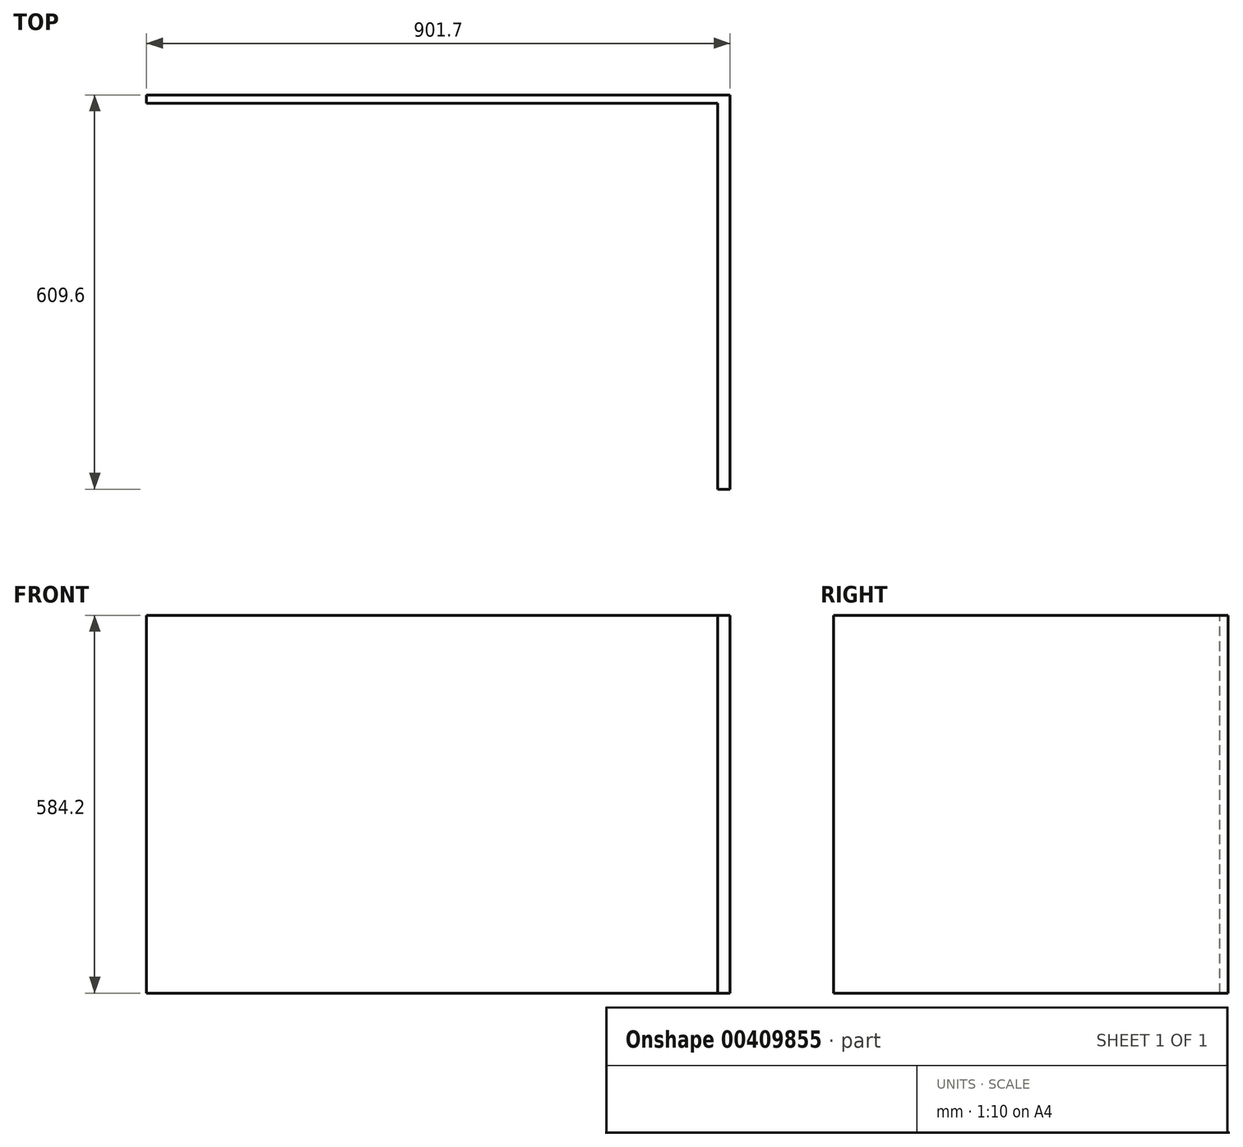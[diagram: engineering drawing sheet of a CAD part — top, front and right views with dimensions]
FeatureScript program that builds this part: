
annotation { "Feature Type Name" : "Feature", "Feature Type Description" : "" }
export const myFeature = defineFeature(function(context is Context, id is Id, definition is map)
    precondition{}
    {
        {
            var Q0;
            Q0=qCreatedBy(makeId("Front.planeOp"),FACE);
            var sketch = newSketch(context, id + "F0", { "sketchPlane" : qUnion([Q0])});
            skLineSegment(sketch, "E0.bottom", {"start": v(0, 0) * mm, "end": v(889, 0) * mm});
            skLineSegment(sketch, "E0.top", {"start": v(0, 584.2) * mm, "end": v(889, 584.2) * mm});
            skLineSegment(sketch, "E0.left", {"start": v(0, 0) * mm, "end": v(0, 584.2) * mm});
            skLineSegment(sketch, "E0.right", {"start": v(889, 0) * mm, "end": v(889, 584.2) * mm});
            skSolve(sketch);
        }
        {
            var Q0;
            Q0=makeQuery(id+"F0.imprint","IMPRINT",FACE,{"disambiguationData":[TD([[makeQuery(id+"F0.imprint","IMPRINT",EDGE,{"derivedFrom":sQuery(id+"F0.wireOp",EDGE,"E0.bottom")}),1.0]])]});
            extrude(context, id + "F1", {"entities" : qUnion([Q0]), "depth" : 12.7 * mm});
        }
        {
            var Q0;
            Q0=qCreatedBy(makeId("Top.planeOp"),FACE);
            var sketch = newSketch(context, id + "F2", { "sketchPlane" : qUnion([Q0])});
            skLineSegment(sketch, "E1", {"start": v(889, 0) * mm, "end": v(901.7, 0) * mm});
            skLineSegment(sketch, "E2", {"start": v(901.7, 0) * mm, "end": v(901.7, -609.6) * mm});
            skLineSegment(sketch, "E3", {"start": v(901.7, -609.6) * mm, "end": v(882.65, -609.6) * mm});
            skLineSegment(sketch, "E4", {"start": v(882.65, -609.6) * mm, "end": v(882.65, -12.7) * mm});
            skLineSegment(sketch, "E5", {"start": v(889, -12.7) * mm, "end": v(889, 0) * mm});
            skLineSegment(sketch, "E6", {"start": v(889, -12.7) * mm, "end": v(882.65, -12.7) * mm});
            skSolve(sketch);
        }
        {
            var Q0;
            Q0 = qSketchRegion(id + "F2", true);
            extrude(context, id + "F3", {"entities" : qUnion([Q0]), "operationType" : NewBodyOperationType.ADD, "depth" : 584.2 * mm});
        }
    });
